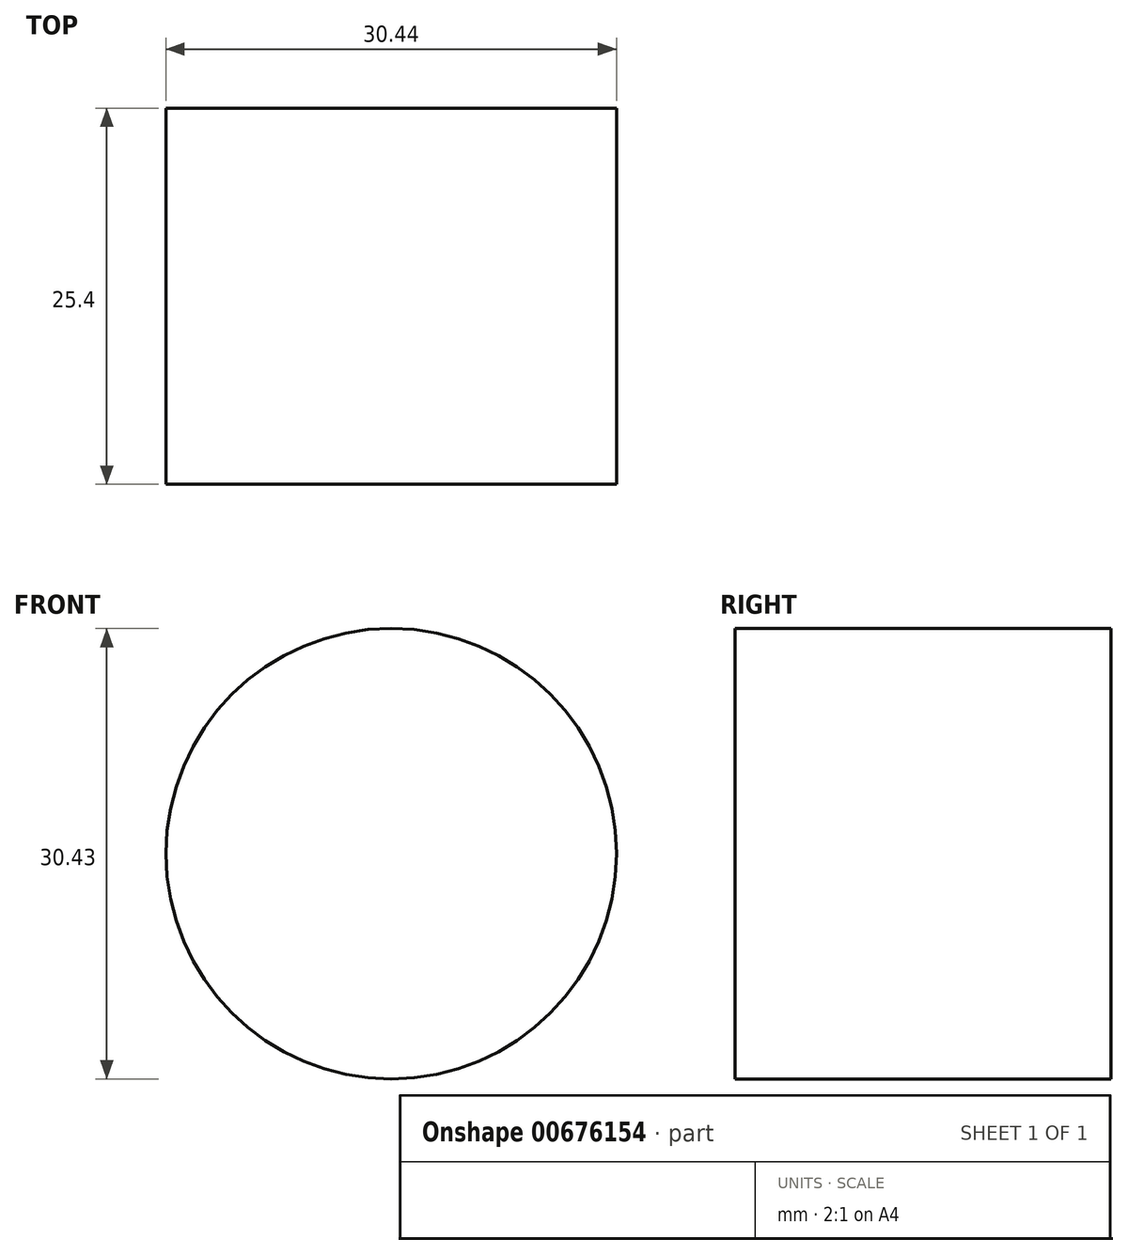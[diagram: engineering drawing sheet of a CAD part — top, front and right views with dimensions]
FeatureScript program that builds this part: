
annotation { "Feature Type Name" : "Feature", "Feature Type Description" : "" }
export const myFeature = defineFeature(function(context is Context, id is Id, definition is map)
    precondition{}
    {
        {
            var Q0;
            Q0=qCreatedBy(makeId("Front.planeOp"),FACE);
            var sketch = newSketch(context, id + "F0", { "sketchPlane" : qUnion([Q0])});
            skCircle(sketch, "E0", {"center": v(-38.38, 35.27) * mm, "radius": 15.22 * mm});
            skSolve(sketch);
        }
        {
            var Q0;
            Q0 = qSketchRegion(id + "F0", true);
            extrude(context, id + "F1", {"entities" : qUnion([Q0]), "depth" : 25.4 * mm, "offsetDistance" : 25.4 * mm});
        }
    });
